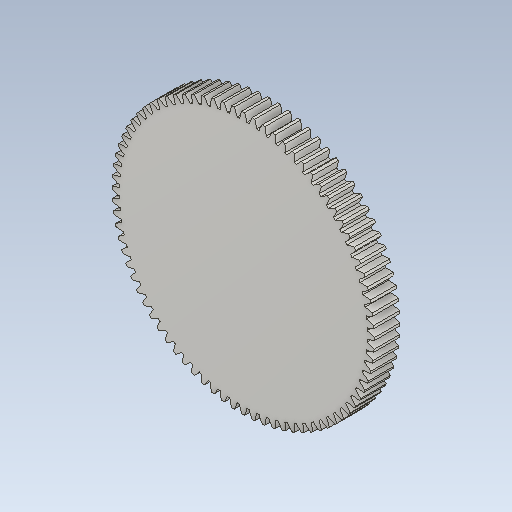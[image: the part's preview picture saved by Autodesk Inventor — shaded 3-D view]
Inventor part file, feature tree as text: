
AUTODESK INVENTOR PART (.ipt)
format: ipt  version: 2020 (Build 240168000, 168)  size: 465,920 bytes
history: native  units: mm (DEFAULTED — no unit token found)
features: plane x3, other x3, sketch x2, extrude x1
ambient origin geometry x8: Origin, YZ Plane, XZ Plane, XY Plane, X Axis, Y Axis, Z Axis, Center Point
bodies: Solid1 (feature_tree)
feature tree (9):
  extrude  "Extrusion1"  Depth=20.0mm TaperAngle=0.0deg
  plane  "Work Plane2"
  plane  "Work Plane8"
  plane  "Work Plane9"
  other  "Spur Gear"
  sketch  "Sketch1"  dims[d0=205.0mm d1=20.0mm d2=0.0mm]
  sketch  "Sketch2"  dims[d3=200.0mm d4=10.0mm d5=0.0mm d16=125.0mm d17=0.0mm d34=0.392699mm d39=0.0mm d41=0.0mm d43=125.0mm d46=125.0mm d47=0.0mm d48=0.0mm]
  other  "Srf1"
  other  "Pitch Diameter"
